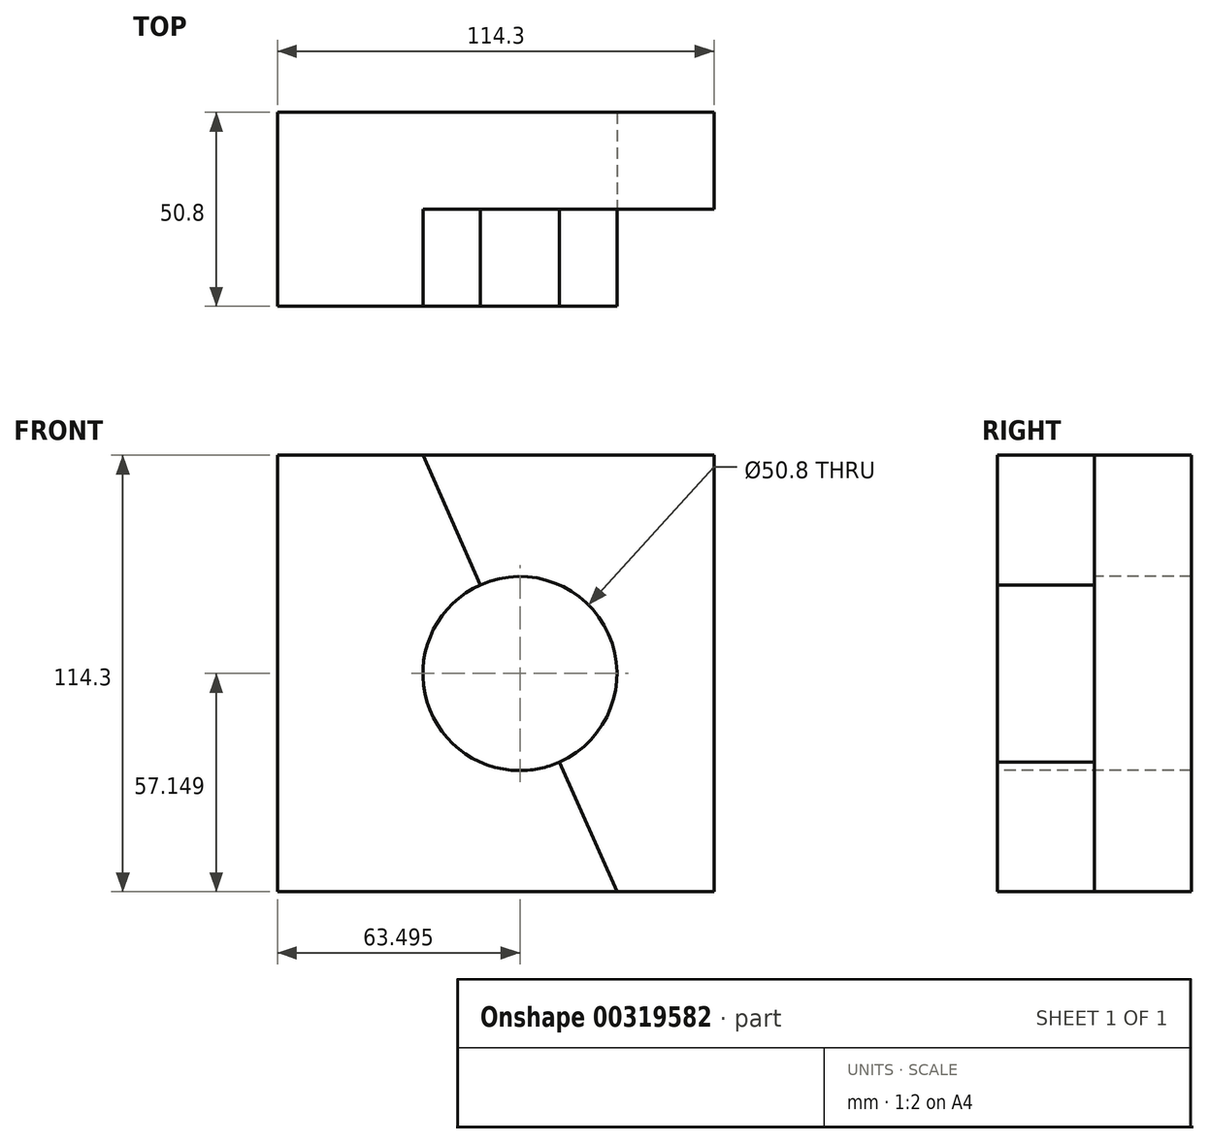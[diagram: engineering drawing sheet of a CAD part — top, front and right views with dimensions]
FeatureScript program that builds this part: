
annotation { "Feature Type Name" : "Feature", "Feature Type Description" : "" }
export const myFeature = defineFeature(function(context is Context, id is Id, definition is map)
    precondition{}
    {
        {
            var Q0;
            Q0=qCreatedBy(makeId("Front.planeOp"),FACE);
            var sketch = newSketch(context, id + "F0", { "sketchPlane" : qUnion([Q0])});
            skLineSegment(sketch, "E0", {"start": v(-50.8, -67.38) * mm, "end": v(63.5, -67.38) * mm});
            skLineSegment(sketch, "E1", {"start": v(63.5, -67.38) * mm, "end": v(63.5, 46.92) * mm});
            skLineSegment(sketch, "E2", {"start": v(63.5, 46.92) * mm, "end": v(-50.8, 46.92) * mm});
            skLineSegment(sketch, "E3", {"start": v(-50.8, 46.92) * mm, "end": v(-50.8, -67.38) * mm});
            skSolve(sketch);
        }
        {
            var Q0;
            Q0=makeQuery(id+"F0.imprint","IMPRINT",FACE,{"disambiguationData":[TD([[makeQuery(id+"F0.imprint","IMPRINT",EDGE,{"derivedFrom":sQuery(id+"F0.wireOp",EDGE,"E0")}),1.0]])]});
            extrude(context, id + "F1", {"entities" : qUnion([Q0]), "depth" : 25.4 * mm});
        }
        {
            var Q0;
            Q0=makeQuery(id+"F1.opExtrude","CAP_FACE",FACE,{"disambiguationData":[OSD([sQuery(id+"F0.wireOp",EDGE,"E0"),sQuery(id+"F0.wireOp",EDGE,"E1"),sQuery(id+"F0.wireOp",EDGE,"E2"),sQuery(id+"F0.wireOp",EDGE,"E3")])],"isStart":false});
            var sketch = newSketch(context, id + "F2", { "sketchPlane" : qUnion([Q0])});
            skLineSegment(sketch, "E4", {"start": v(-50.8, 46.92) * mm, "end": v(-50.8, -67.38) * mm});
            skLineSegment(sketch, "E5", {"start": v(-50.8, 46.92) * mm, "end": v(-12.7, 46.92) * mm});
            skLineSegment(sketch, "E6", {"start": v(-50.8, -67.38) * mm, "end": v(38.1, -67.38) * mm});
            skLineSegment(sketch, "E7", {"start": v(-12.7, 46.92) * mm, "end": v(38.1, -67.38) * mm});
            skSolve(sketch);
        }
        {
            var Q0;
            Q0=makeQuery(id+"F2.imprint","IMPRINT",FACE,{"disambiguationData":[TD([[makeQuery(id+"F2.imprint","IMPRINT",EDGE,{"derivedFrom":sQuery(id+"F2.wireOp",EDGE,"E4")}),1.0]])]});
            extrude(context, id + "F3", {"entities" : qUnion([Q0]), "operationType" : NewBodyOperationType.ADD, "depth" : 25.4 * mm});
        }
        {
            var Q0;
            Q0=makeQuery(id+"F3.opExtrude","CAP_FACE",FACE,{"disambiguationData":[OSD([sQuery(id+"F2.wireOp",EDGE,"E4"),sQuery(id+"F2.wireOp",EDGE,"E5"),sQuery(id+"F2.wireOp",EDGE,"E6"),sQuery(id+"F2.wireOp",EDGE,"E7")])],"isStart":false});
            var sketch = newSketch(context, id + "F4", { "sketchPlane" : qUnion([Q0])});
            skCircle(sketch, "E8", {"center": v(12.7, -10.23) * mm, "radius": 25.4 * mm});
            skSolve(sketch);
        }
        {
            var Q0;
            {var subQ0=sQuery(id+"F4.wireOp",EDGE,"E8");var subQ1=makeQuery(id+"F3.opExtrude","CAP_EDGE",EDGE,{"disambiguationData":[OSD([sQuery(id+"F2.wireOp",EDGE,"E7")])],"isStart":false});var subQ2=makeQuery(id+"F4.imprint","INTERSECT",VERTEX,{"disambiguationData":[OD(0.0)],"derivedFrom":[subQ1,subQ0]});Q0=makeQuery(id+"F4.imprint","IMPRINT",FACE,{"disambiguationData":[TD([[makeQuery(id+"F4.imprint","IMPRINT",EDGE,{"disambiguationData":[TD([[subQ2,-1.0]])],"derivedFrom":subQ0}),1.0]])]});}
            var Q1;
            {var subQ0=sQuery(id+"F4.wireOp",EDGE,"E8");var subQ1=makeQuery(id+"F3.opExtrude","CAP_EDGE",EDGE,{"disambiguationData":[OSD([sQuery(id+"F2.wireOp",EDGE,"E7")])],"isStart":false});var subQ2=makeQuery(id+"F4.imprint","INTERSECT",VERTEX,{"disambiguationData":[OD(0.0)],"derivedFrom":[subQ1,subQ0]});Q1=makeQuery(id+"F4.imprint","IMPRINT",FACE,{"disambiguationData":[TD([[makeQuery(id+"F4.imprint","IMPRINT",EDGE,{"disambiguationData":[TD([[subQ2,1.0]])],"derivedFrom":subQ0}),1.0]])]});}
            extrude(context, id + "F5", {"entities" : qUnion([Q0, Q1]), "operationType" : NewBodyOperationType.REMOVE, "endBound" : BoundingType.THROUGH_ALL, "oppositeDirection" : true, "depth" : 25.4 * mm});
        }
    });
